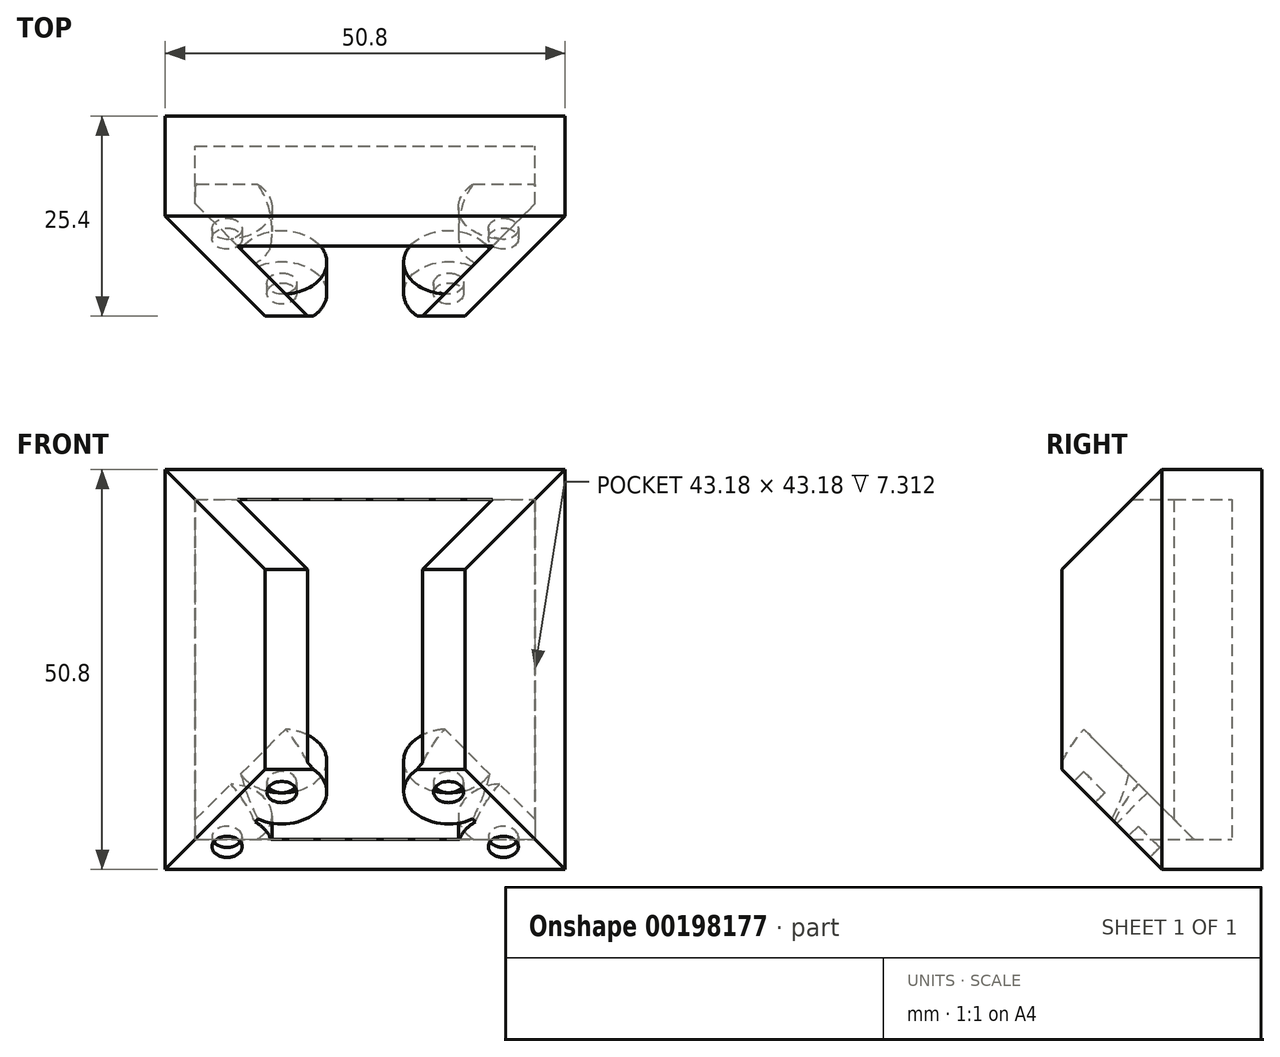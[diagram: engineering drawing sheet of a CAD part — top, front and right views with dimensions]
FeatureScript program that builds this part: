
annotation { "Feature Type Name" : "Feature", "Feature Type Description" : "" }
export const myFeature = defineFeature(function(context is Context, id is Id, definition is map)
    precondition{}
    {
        {
            var Q0;
            Q0=qCreatedBy(makeId("Front.planeOp"),FACE);
            var sketch = newSketch(context, id + "F0", { "sketchPlane" : qUnion([Q0])});
            skLineSegment(sketch, "E0.bottom", {"start": v(-23.39, 25.4) * mm, "end": v(27.41, 25.4) * mm});
            skLineSegment(sketch, "E0.top", {"start": v(-23.39, -25.4) * mm, "end": v(27.41, -25.4) * mm});
            skLineSegment(sketch, "E0.left", {"start": v(-23.39, 25.4) * mm, "end": v(-23.39, -25.4) * mm});
            skLineSegment(sketch, "E0.right", {"start": v(27.41, 25.4) * mm, "end": v(27.41, -25.4) * mm});
            skLineSegment(sketch, "E1", {"start": v(27.41, 0) * mm, "end": v(-23.39, 0) * mm, "construction": true});
            skSolve(sketch);
        }
        {
            var Q0;
            Q0 = qSketchRegion(id + "F0", true);
            extrude(context, id + "F1", {"entities" : qUnion([Q0]), "depth" : 25.4 * mm});
        }
        {
            var Q0;
            Q0=makeQuery(id+"F1.opExtrude","CAP_EDGE",EDGE,{"disambiguationData":[OSD([sQuery(id+"F0.wireOp",EDGE,"E0.bottom")])],"isStart":false});
            var Q1;
            Q1=makeQuery(id+"F1.opExtrude","CAP_EDGE",EDGE,{"disambiguationData":[OSD([sQuery(id+"F0.wireOp",EDGE,"E0.right")])],"isStart":false});
            var Q2;
            Q2=makeQuery(id+"F1.opExtrude","CAP_EDGE",EDGE,{"disambiguationData":[OSD([sQuery(id+"F0.wireOp",EDGE,"E0.top")])],"isStart":false});
            var Q3;
            Q3=makeQuery(id+"F1.opExtrude","CAP_EDGE",EDGE,{"disambiguationData":[OSD([sQuery(id+"F0.wireOp",EDGE,"E0.left")])],"isStart":false});
            chamfer(context, id + "F2", {"entities" : qUnion([Q0, Q1, Q2, Q3]), "width" : 12.7 * mm, "tangentPropagation" : true});
        }
        {
            var Q0;
            Q0=makeQuery(id+"F2.opChamfer","BLEND_FACE",FACE,{"disambiguationData":[OSD([sQuery(id+"F0.wireOp",EDGE,"E0.top")])]});
            var sketch = newSketch(context, id + "F3", { "sketchPlane" : qUnion([Q0])});
            skCircle(sketch, "E2", {"center": v(12.6, 4.92) * mm, "radius": 1.9 * mm});
            skCircle(sketch, "E3", {"center": v(-8.59, 4.92) * mm, "radius": 1.9 * mm});
            skCircle(sketch, "E4", {"center": v(19.56, -4.92) * mm, "radius": 1.9 * mm});
            skCircle(sketch, "E5", {"center": v(-15.54, -4.92) * mm, "radius": 1.9 * mm});
            skLineSegment(sketch, "E6.0", {"start": v(-10.69, 8.98) * mm, "end": v(14.71, 8.98) * mm});
            skLineSegment(sketch, "E6.1", {"start": v(27.41, -8.98) * mm, "end": v(14.71, 8.98) * mm});
            skLineSegment(sketch, "E6.2", {"start": v(27.41, -8.98) * mm, "end": v(-23.39, -8.98) * mm});
            skLineSegment(sketch, "E6.3", {"start": v(-23.39, -8.98) * mm, "end": v(-10.69, 8.98) * mm});
            skLineSegment(sketch, "E7.0", {"start": v(-8.59, 4.92) * mm, "end": v(12.6, 4.92) * mm, "construction": true});
            skLineSegment(sketch, "E7.1", {"start": v(-15.54, -4.92) * mm, "end": v(-8.59, 4.92) * mm, "construction": true});
            skLineSegment(sketch, "E7.2", {"start": v(19.56, -4.92) * mm, "end": v(-15.54, -4.92) * mm, "construction": true});
            skLineSegment(sketch, "E7.3", {"start": v(19.56, -4.92) * mm, "end": v(12.6, 4.92) * mm, "construction": true});
            skSolve(sketch);
        }
        {
            var Q0;
            Q0=makeQuery(id+"F3.imprint","IMPRINT",FACE,{"disambiguationData":[TD([[makeQuery(id+"F3.imprint","IMPRINT",EDGE,{"derivedFrom":sQuery(id+"F3.wireOp",EDGE,"E3")}),1.0]])]});
            var Q1;
            Q1=makeQuery(id+"F3.imprint","IMPRINT",FACE,{"disambiguationData":[TD([[makeQuery(id+"F3.imprint","IMPRINT",EDGE,{"derivedFrom":sQuery(id+"F3.wireOp",EDGE,"E2")}),1.0]])]});
            var Q2;
            Q2=makeQuery(id+"F3.imprint","IMPRINT",FACE,{"disambiguationData":[TD([[makeQuery(id+"F3.imprint","IMPRINT",EDGE,{"derivedFrom":sQuery(id+"F3.wireOp",EDGE,"E4")}),1.0]])]});
            var Q3;
            Q3=makeQuery(id+"F3.imprint","IMPRINT",FACE,{"disambiguationData":[TD([[makeQuery(id+"F3.imprint","IMPRINT",EDGE,{"derivedFrom":sQuery(id+"F3.wireOp",EDGE,"E5")}),1.0]])]});
            extrude(context, id + "F4", {"entities" : qUnion([Q0, Q1, Q2, Q3]), "operationType" : NewBodyOperationType.REMOVE, "oppositeDirection" : true, "depth" : 1.78 * mm});
        }
        {
            var Q0;
            Q0=sQuery(id+"F0.wireOp",EDGE,"E1");
            var Q1;
            Q1=makeQuery(id+"F1.opExtrude","SWEPT_EDGE",EDGE,{"disambiguationData":[OSD([sQuery(id+"F0.wireOp",EDGE,"E0.top"),sQuery(id+"F0.wireOp",EDGE,"E0.right")])]});
            cPlane(context, id + "F5", {"entities" : qUnion([Q0, Q1]), "cplaneType" : CPlaneType.LINE_ANGLE, "offset" : 25.4 * mm, "angle" : 0 * degree, "width" : 152.4 * mm, "height" : 152.4 * mm});
        }
        {
            var Q0;
            Q0=makeQuery(id+"F2.opChamfer","BLEND_FACE",FACE,{"disambiguationData":[OSD([sQuery(id+"F0.wireOp",EDGE,"E0.bottom")])]});
            var Q1;
            Q1=makeQuery(id+"F2.opChamfer","BLEND_FACE",FACE,{"disambiguationData":[OSD([sQuery(id+"F0.wireOp",EDGE,"E0.top")])]});
            var Q2;
            Q2=makeQuery(id+"F1.opExtrude","CAP_FACE",FACE,{"disambiguationData":[OSD([sQuery(id+"F0.wireOp",EDGE,"E0.bottom"),sQuery(id+"F0.wireOp",EDGE,"E0.top"),sQuery(id+"F0.wireOp",EDGE,"E0.left"),sQuery(id+"F0.wireOp",EDGE,"E0.right")])],"isStart":false});
            shell(context, id + "F6", {"entities" : qUnion([Q0, Q1, Q2]), "thickness" : 3.8 * mm});
        }
    });
